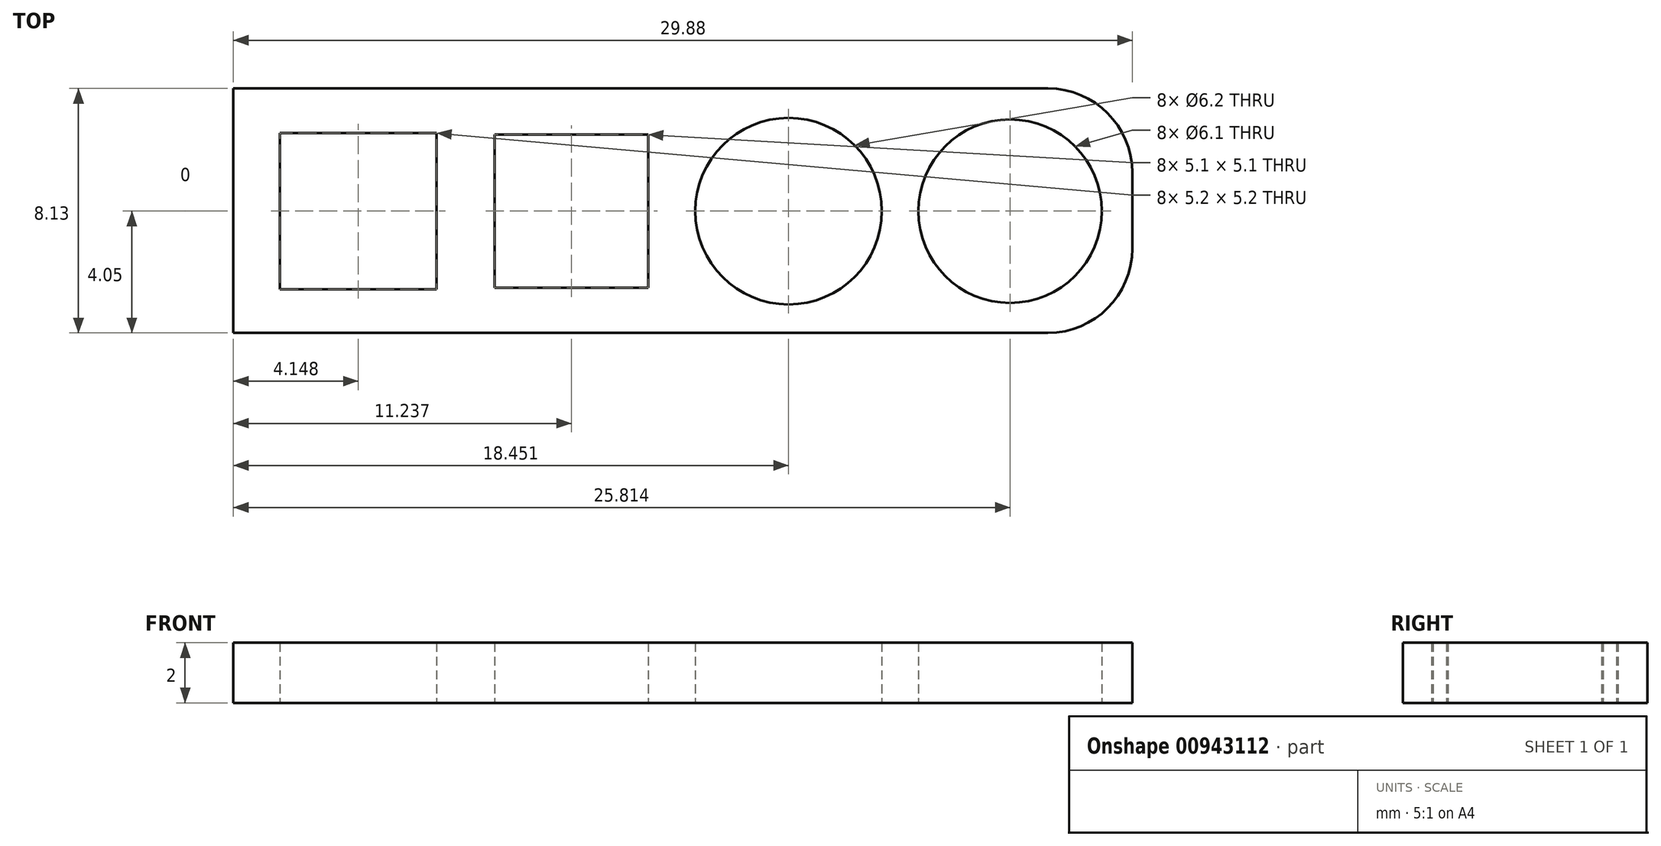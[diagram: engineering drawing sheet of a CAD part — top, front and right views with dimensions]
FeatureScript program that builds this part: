
annotation { "Feature Type Name" : "Feature", "Feature Type Description" : "" }
export const myFeature = defineFeature(function(context is Context, id is Id, definition is map)
    precondition{}
    {
        {
            var Q0;
            Q0=qCreatedBy(makeId("Top.planeOp"),FACE);
            var sketch = newSketch(context, id + "F0", { "sketchPlane" : qUnion([Q0])});
            skCircle(sketch, "E0", {"center": v(-18.94, 0) * mm, "radius": 3.05 * mm});
            skCircle(sketch, "E1", {"center": v(-26.3, 0) * mm, "radius": 3.1 * mm});
            skLineSegment(sketch, "E2.bottom", {"start": v(-30.96, -2.55) * mm, "end": v(-36.06, -2.55) * mm});
            skLineSegment(sketch, "E2.top", {"start": v(-30.96, 2.55) * mm, "end": v(-36.06, 2.55) * mm});
            skLineSegment(sketch, "E2.left", {"start": v(-30.96, -2.55) * mm, "end": v(-30.96, 2.55) * mm});
            skLineSegment(sketch, "E2.right", {"start": v(-36.06, -2.55) * mm, "end": v(-36.06, 2.55) * mm});
            skPoint(sketch, "E2.middle", {"position": v(-33.51, 0) * mm});
            skLineSegment(sketch, "E3.bottom", {"start": v(-43.2, -2.6) * mm, "end": v(-38, -2.6) * mm});
            skLineSegment(sketch, "E3.top", {"start": v(-43.2, 2.6) * mm, "end": v(-38, 2.6) * mm});
            skLineSegment(sketch, "E3.left", {"start": v(-43.2, -2.6) * mm, "end": v(-43.2, 2.6) * mm});
            skLineSegment(sketch, "E3.right", {"start": v(-38, -2.6) * mm, "end": v(-38, 2.6) * mm});
            skPoint(sketch, "E3.middle", {"position": v(-40.6, 0) * mm});
            skLineSegment(sketch, "E4.bottom", {"start": v(-44.75, 4.08) * mm, "end": v(-17.67, 4.08) * mm});
            skLineSegment(sketch, "E4.top", {"start": v(-44.75, -4.05) * mm, "end": v(-17.67, -4.05) * mm});
            skLineSegment(sketch, "E4.left", {"start": v(-44.75, 4.08) * mm, "end": v(-44.75, -4.05) * mm});
            skLineSegment(sketch, "E4.right", {"start": v(-14.87, 1.28) * mm, "end": v(-14.87, -1.25) * mm});
            skPoint(sketch, "E5.visualSharp", {"position": v(-14.87, 4.08) * mm});
            skArc(sketch, "E5.filletArc", {"start": v(-14.87, 1.28) * mm, "mid": v(-15.7, 3.26) * mm, "end": v(-17.67, 4.08) * mm});
            skPoint(sketch, "E6.visualSharp", {"position": v(-14.87, -4.05) * mm});
            skArc(sketch, "E6.filletArc", {"start": v(-17.67, -4.05) * mm, "mid": v(-15.7, -3.23) * mm, "end": v(-14.87, -1.25) * mm});
            skSolve(sketch);
        }
        {
            var Q0;
            Q0=qSketchRegion(id+"F0",true);
            extrude(context, id + "F1", {"entities" : qUnion([Q0]), "depth" : 2 * mm, "offsetDistance" : 25 * mm});
        }
    });
